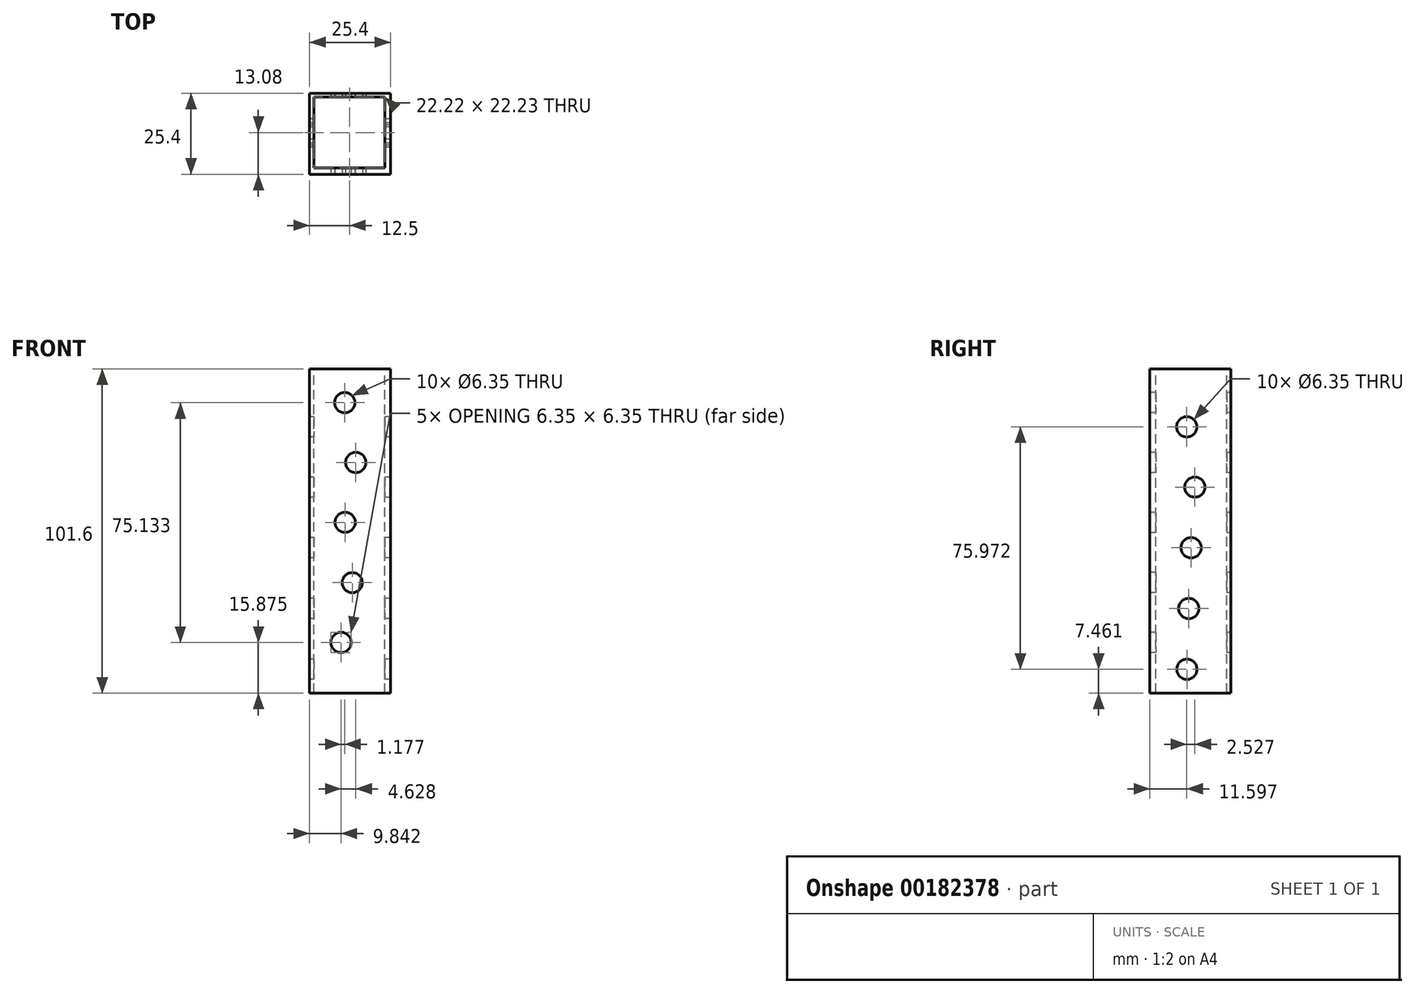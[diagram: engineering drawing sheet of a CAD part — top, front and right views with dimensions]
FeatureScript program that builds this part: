
annotation { "Feature Type Name" : "Feature", "Feature Type Description" : "" }
export const myFeature = defineFeature(function(context is Context, id is Id, definition is map)
    precondition{}
    {
        {
            var Q0;
            Q0=qCreatedBy(makeId("Top.planeOp"),FACE);
            var sketch = newSketch(context, id + "F0", { "sketchPlane" : qUnion([Q0])});
            skLineSegment(sketch, "E0.bottom", {"start": v(0, 0) * mm, "end": v(-25.4, 0) * mm});
            skLineSegment(sketch, "E0.top", {"start": v(0, -25.4) * mm, "end": v(-25.4, -25.4) * mm});
            skLineSegment(sketch, "E0.left", {"start": v(0, 0) * mm, "end": v(0, -25.4) * mm});
            skLineSegment(sketch, "E0.right", {"start": v(-25.4, 0) * mm, "end": v(-25.4, -25.4) * mm});
            skSolve(sketch);
        }
        {
            var Q0;
            Q0 = qSketchRegion(id + "F0", true);
            extrude(context, id + "F1", {"entities" : qUnion([Q0]), "depth" : 101.6 * mm});
        }
        {
            var Q0;
            Q0=makeQuery(id+"F1.opExtrude","CAP_FACE",FACE,{"disambiguationData":[OSD([sQuery(id+"F0.wireOp",EDGE,"E0.bottom"),sQuery(id+"F0.wireOp",EDGE,"E0.top"),sQuery(id+"F0.wireOp",EDGE,"E0.left"),sQuery(id+"F0.wireOp",EDGE,"E0.right")])],"isStart":false});
            var sketch = newSketch(context, id + "F2", { "sketchPlane" : qUnion([Q0])});
            skLineSegment(sketch, "E1.bottom", {"start": v(-1.79, -1.2) * mm, "end": v(-24.01, -1.2) * mm});
            skLineSegment(sketch, "E1.top", {"start": v(-1.79, -23.43) * mm, "end": v(-24.01, -23.43) * mm});
            skLineSegment(sketch, "E1.left", {"start": v(-1.79, -1.2) * mm, "end": v(-1.79, -23.43) * mm});
            skLineSegment(sketch, "E1.right", {"start": v(-24.01, -1.2) * mm, "end": v(-24.01, -23.43) * mm});
            skSolve(sketch);
        }
        {
            var Q0;
            Q0 = qSketchRegion(id + "F2", true);
            extrude(context, id + "F3", {"entities" : qUnion([Q0]), "operationType" : NewBodyOperationType.REMOVE, "oppositeDirection" : true, "depth" : 101.6 * mm});
        }
        {
            var Q0;
            Q0=makeQuery(id+"F1.opExtrude","SWEPT_FACE",FACE,{"disambiguationData":[OSD([sQuery(id+"F0.wireOp",EDGE,"E0.right")])]});
            var sketch = newSketch(context, id + "F4", { "sketchPlane" : qUnion([Q0])});
            skCircle(sketch, "E2", {"center": v(13.78, 7.46) * mm, "radius": 3.17 * mm});
            skSolve(sketch);
        }
        {
            var Q0;
            Q0 = qSketchRegion(id + "F4", true);
            extrude(context, id + "F5", {"entities" : qUnion([Q0]), "operationType" : NewBodyOperationType.REMOVE, "oppositeDirection" : true, "depth" : 25.4 * mm});
        }
        {
            var Q0;
            Q0=makeQuery(id+"F1.opExtrude","SWEPT_FACE",FACE,{"disambiguationData":[OSD([sQuery(id+"F0.wireOp",EDGE,"E0.right")])]});
            var sketch = newSketch(context, id + "F6", { "sketchPlane" : qUnion([Q0])});
            skCircle(sketch, "E3", {"center": v(13.17, 26.5) * mm, "radius": 3.18 * mm});
            skSolve(sketch);
        }
        {
            var Q0;
            Q0 = qSketchRegion(id + "F6", true);
            extrude(context, id + "F7", {"entities" : qUnion([Q0]), "operationType" : NewBodyOperationType.REMOVE, "oppositeDirection" : true, "depth" : 25.4 * mm});
        }
        {
            var Q0;
            Q0=makeQuery(id+"F1.opExtrude","SWEPT_FACE",FACE,{"disambiguationData":[OSD([sQuery(id+"F0.wireOp",EDGE,"E0.right")])]});
            var sketch = newSketch(context, id + "F8", { "sketchPlane" : qUnion([Q0])});
            skCircle(sketch, "E4", {"center": v(12.44, 45.54) * mm, "radius": 3.18 * mm});
            skSolve(sketch);
        }
        {
            var Q0;
            Q0 = qSketchRegion(id + "F8", true);
            extrude(context, id + "F9", {"entities" : qUnion([Q0]), "operationType" : NewBodyOperationType.REMOVE, "oppositeDirection" : true, "depth" : 25.4 * mm});
        }
        {
            var Q0;
            Q0=makeQuery(id+"F1.opExtrude","SWEPT_FACE",FACE,{"disambiguationData":[OSD([sQuery(id+"F0.wireOp",EDGE,"E0.right")])]});
            var sketch = newSketch(context, id + "F10", { "sketchPlane" : qUnion([Q0])});
            skCircle(sketch, "E5", {"center": v(11.28, 64.55) * mm, "radius": 3.18 * mm});
            skSolve(sketch);
        }
        {
            var Q0;
            Q0 = qSketchRegion(id + "F10", true);
            extrude(context, id + "F11", {"entities" : qUnion([Q0]), "operationType" : NewBodyOperationType.REMOVE, "oppositeDirection" : true, "depth" : 25.4 * mm});
        }
        {
            var Q0;
            Q0=makeQuery(id+"F1.opExtrude","SWEPT_FACE",FACE,{"disambiguationData":[OSD([sQuery(id+"F0.wireOp",EDGE,"E0.right")])]});
            var sketch = newSketch(context, id + "F12", { "sketchPlane" : qUnion([Q0])});
            skCircle(sketch, "E6", {"center": v(13.8, 83.43) * mm, "radius": 3.18 * mm});
            skSolve(sketch);
        }
        {
            var Q0;
            Q0 = qSketchRegion(id + "F12", true);
            extrude(context, id + "F13", {"entities" : qUnion([Q0]), "operationType" : NewBodyOperationType.REMOVE, "oppositeDirection" : true, "depth" : 25.4 * mm});
        }
        {
            var Q0;
            Q0=makeQuery(id+"F1.opExtrude","SWEPT_FACE",FACE,{"disambiguationData":[OSD([sQuery(id+"F0.wireOp",EDGE,"E0.top")])]});
            var sketch = newSketch(context, id + "F14", { "sketchPlane" : qUnion([Q0])});
            skCircle(sketch, "E7", {"center": v(-15.56, 15.88) * mm, "radius": 3.18 * mm});
            skSolve(sketch);
        }
        {
            var Q0;
            Q0 = qSketchRegion(id + "F14", true);
            extrude(context, id + "F15", {"entities" : qUnion([Q0]), "operationType" : NewBodyOperationType.REMOVE, "oppositeDirection" : true, "depth" : 25.4 * mm});
        }
        {
            var Q0;
            Q0=makeQuery(id+"F1.opExtrude","SWEPT_FACE",FACE,{"disambiguationData":[OSD([sQuery(id+"F0.wireOp",EDGE,"E0.top")])]});
            var sketch = newSketch(context, id + "F16", { "sketchPlane" : qUnion([Q0])});
            skCircle(sketch, "E8", {"center": v(-12.04, 34.6) * mm, "radius": 3.18 * mm});
            skSolve(sketch);
        }
        {
            var Q0;
            Q0 = qSketchRegion(id + "F16", true);
            extrude(context, id + "F17", {"entities" : qUnion([Q0]), "operationType" : NewBodyOperationType.REMOVE, "oppositeDirection" : true, "depth" : 25.4 * mm});
        }
        {
            var Q0;
            Q0=makeQuery(id+"F1.opExtrude","SWEPT_FACE",FACE,{"disambiguationData":[OSD([sQuery(id+"F0.wireOp",EDGE,"E0.top")])]});
            var sketch = newSketch(context, id + "F18", { "sketchPlane" : qUnion([Q0])});
            skCircle(sketch, "E9", {"center": v(-14.26, 53.52) * mm, "radius": 3.18 * mm});
            skSolve(sketch);
        }
        {
            var Q0;
            Q0 = qSketchRegion(id + "F18", true);
            extrude(context, id + "F19", {"entities" : qUnion([Q0]), "operationType" : NewBodyOperationType.REMOVE, "oppositeDirection" : true, "depth" : 25.4 * mm});
        }
        {
            var Q0;
            Q0=makeQuery(id+"F1.opExtrude","SWEPT_FACE",FACE,{"disambiguationData":[OSD([sQuery(id+"F0.wireOp",EDGE,"E0.top")])]});
            var sketch = newSketch(context, id + "F20", { "sketchPlane" : qUnion([Q0])});
            skCircle(sketch, "E10", {"center": v(-10.93, 72.27) * mm, "radius": 3.18 * mm});
            skSolve(sketch);
        }
        {
            var Q0;
            Q0 = qSketchRegion(id + "F20", true);
            extrude(context, id + "F21", {"entities" : qUnion([Q0]), "operationType" : NewBodyOperationType.REMOVE, "oppositeDirection" : true, "depth" : 25.4 * mm});
        }
        {
            var Q0;
            Q0=makeQuery(id+"F1.opExtrude","SWEPT_FACE",FACE,{"disambiguationData":[OSD([sQuery(id+"F0.wireOp",EDGE,"E0.top")])]});
            var sketch = newSketch(context, id + "F22", { "sketchPlane" : qUnion([Q0])});
            skCircle(sketch, "E11", {"center": v(-14.38, 91) * mm, "radius": 3.18 * mm});
            skSolve(sketch);
        }
        {
            var Q0;
            Q0 = qSketchRegion(id + "F22", true);
            extrude(context, id + "F23", {"entities" : qUnion([Q0]), "operationType" : NewBodyOperationType.REMOVE, "oppositeDirection" : true, "depth" : 25.4 * mm});
        }
    });
